# Revit family: Eurolan_Полка выдвижная до 30 кг
name_source: partatom
category: Устройства связи
units: mm (PartAtom-declared; Revit-internal decimal feet)

## family parameters
Всегда вертикально = Да
На основе рабочей плоскости = Нет
Общий = Нет
При загрузке вырезать с полостями = Нет
Размер круглого соединителя = Использовать диаметр
Сохранять ориентацию аннотаций = Нет
Тип детали = Нормальный
Точка расчета площади = Нет

## types (5) — shared parameters
ADSK_Единица измерения = шт
ADSK_Завод-изготовитель = Eurolan
ADSK_Количество = 1
ADSK_Марка = 30
ADSK_Материал = Черный антрацит
ADSK_Наименование краткое = Полка выдвижная до 30 кг

## per-type parameters (varying)
| type | ADSK_Код изделия | ADSK_Масса | ADSK_Наименование | Выбор_графики |
| Полка выдвижная до 30 кг_450 мм | 60A-03-45-11BL | 4 | Полка выдвижная до 30 кг, 450 мм | Полка выдвижная : 450 |
| Полка выдвижная до 30 кг_580 мм | 60A-03-58-11BL | 5 | Полка выдвижная до 30 кг, 580 мм | Полка выдвижная : 580 |
| Полка выдвижная до 30 кг_750 мм | 60A-03-75-11BL | 6.3 | Полка выдвижная до 30 кг, 750 мм | Полка выдвижная : 750 |
| Полка выдвижная до 30 кг_620 мм | 60A-03-62-11BL | 5.2 | Полка выдвижная до 30 кг, 620 мм | Полка выдвижная : 620 |
| Полка выдвижная до 30 кг_1000 мм | 60A-03-1A-11BL | 8.2 | Полка выдвижная до 30 кг, 1000 мм | Полка выдвижная : 1000 |
